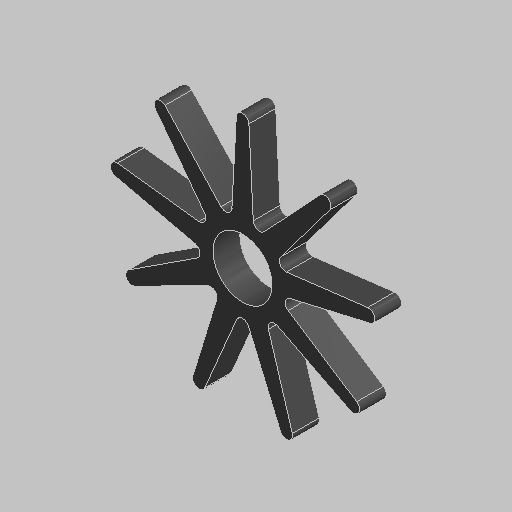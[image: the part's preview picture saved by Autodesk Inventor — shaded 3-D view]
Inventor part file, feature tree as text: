
AUTODESK INVENTOR PART (.ipt)
format: ipt  version: 2023.5 (Build 275446000, 446)  size: 115,712 bytes
history: native  units: mm (DEFAULTED — no unit token found)
features: fillet x1
ambient origin geometry x8: Origin, YZ Plane, XZ Plane, XY Plane, X Axis, Y Axis, Z Axis, Center Point
bodies: Solid1 (feature_tree)
feature tree (1):
  fillet  "Fillet1"  [1 undecoded]
note: 1 required parameter value undecoded (feature->parameter linkage not recoverable at this tier; creation-order binding heuristic only, values carry confidence <= 0.55)
